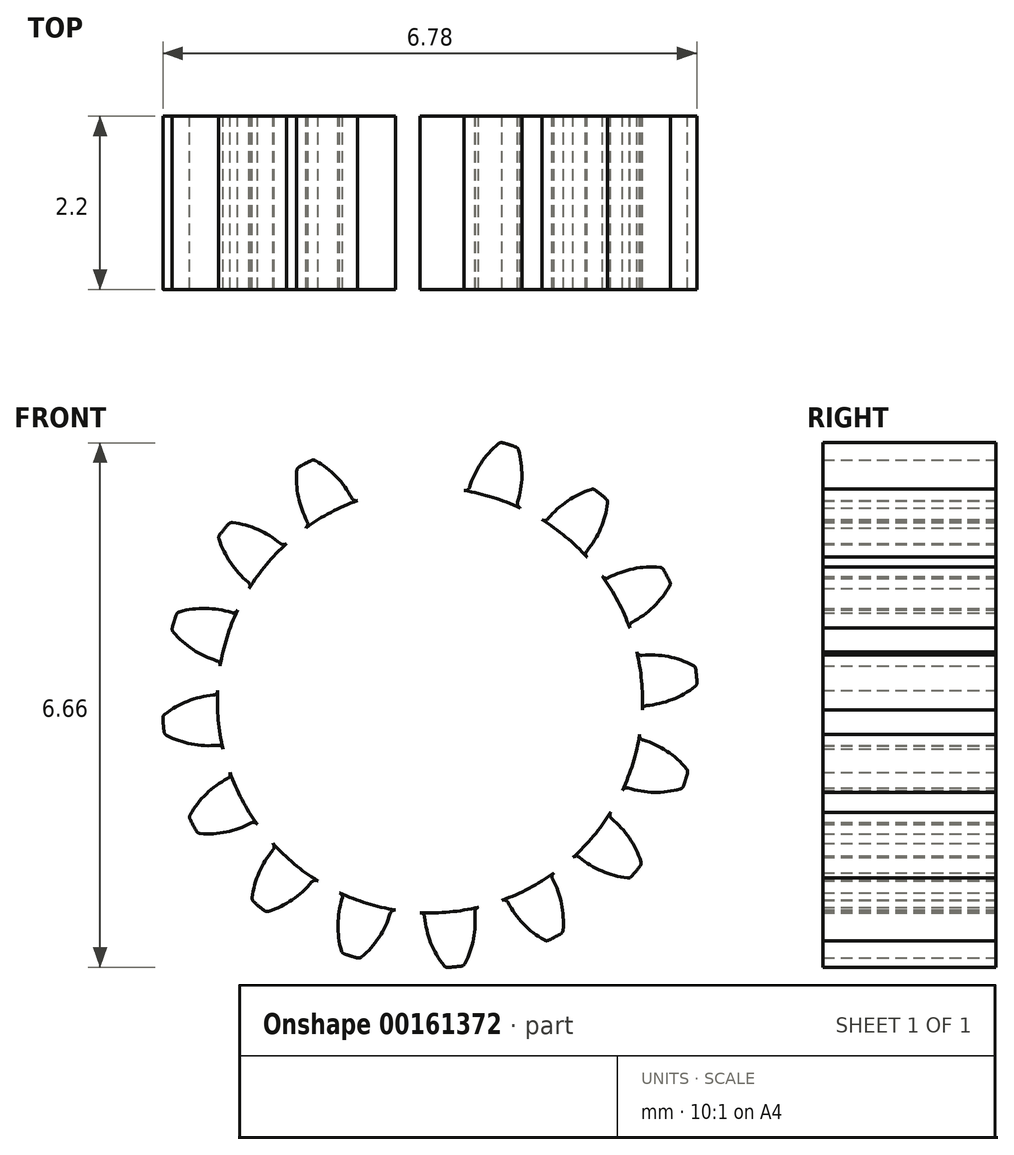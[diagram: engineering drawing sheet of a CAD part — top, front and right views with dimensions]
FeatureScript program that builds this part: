
annotation { "Feature Type Name" : "Feature", "Feature Type Description" : "" }
export const myFeature = defineFeature(function(context is Context, id is Id, definition is map)
    precondition{}
    {
        {
            var Q0;
            Q0=qCreatedBy(makeId("Front.planeOp"),FACE);
            var sketch = newSketch(context, id + "F0", { "sketchPlane" : qUnion([Q0])});
            skCircle(sketch, "E0", {"center": v(0, 0) * mm, "radius": 2.7 * mm, "construction": true});
            skCircle(sketch, "E1", {"center": v(0, 0) * mm, "radius": 3.05 * mm, "construction": true});
            skCircle(sketch, "E2", {"center": v(0, 0) * mm, "radius": 3.4 * mm, "construction": true});
            skLineSegment(sketch, "E3", {"start": v(0, 0) * mm, "end": v(0, 10.28) * mm, "construction": true});
            skLineSegment(sketch, "E4", {"start": v(0, 0) * mm, "end": v(-1.03, 11.12) * mm, "construction": true});
            skLineSegment(sketch, "E5", {"start": v(0, 3.05) * mm, "end": v(-15.76, 3.05) * mm, "construction": true});
            skLineSegment(sketch, "E6", {"start": v(0, 3.05) * mm, "end": v(-14.39, -2.19) * mm, "construction": true});
            skCircle(sketch, "E7", {"center": v(0, 3.05) * mm, "radius": 1.17 * mm, "construction": true});
            skCircle(sketch, "E8", {"center": v(-1.1, 2.65) * mm, "radius": 1.16 * mm, "construction": true});
            skArc(sketch, "E9", {"start": v(-0.18, 3.37) * mm, "mid": v(-0.01, 3.08) * mm, "end": v(0.07, 2.75) * mm});
            skArc(sketch, "E10.MirrorCS", {"start": v(-0.45, 3.34) * mm, "mid": v(-0.56, 3.03) * mm, "end": v(-0.57, 2.7) * mm});
            skArc(sketch, "E11", {"start": v(-0.4, 3.38) * mm, "mid": v(-0.31, 3.39) * mm, "end": v(-0.23, 3.4) * mm});
            skArc(sketch, "E12", {"start": v(-0.62, 2.63) * mm, "mid": v(0.25, -2.69) * mm, "end": v(0.12, 2.7) * mm});
            skPoint(sketch, "E13.visualSharp", {"position": v(-0.56, 2.64) * mm});
            skArc(sketch, "E13.filletArc", {"start": v(-0.62, 2.63) * mm, "mid": v(-0.58, 2.65) * mm, "end": v(-0.57, 2.7) * mm});
            skPoint(sketch, "E14.visualSharp", {"position": v(-0.43, 3.37) * mm});
            skArc(sketch, "E14.filletArc", {"start": v(-0.4, 3.38) * mm, "mid": v(-0.43, 3.37) * mm, "end": v(-0.45, 3.34) * mm});
            skPoint(sketch, "E15.visualSharp", {"position": v(-0.2, 3.4) * mm});
            skArc(sketch, "E15.filletArc", {"start": v(-0.18, 3.37) * mm, "mid": v(-0.2, 3.39) * mm, "end": v(-0.23, 3.4) * mm});
            skPoint(sketch, "E16.visualSharp", {"position": v(0.07, 2.7) * mm});
            skArc(sketch, "E16.filletArc", {"start": v(0.07, 2.75) * mm, "mid": v(0.08, 2.71) * mm, "end": v(0.12, 2.7) * mm});
            skArc(sketch, "E17.1.0", {"start": v(-1.58, 2.2) * mm, "mid": v(-1.55, 2.23) * mm, "end": v(-1.56, 2.27) * mm});
            skArc(sketch, "E17.1.1", {"start": v(-1.7, 2.92) * mm, "mid": v(-1.67, 2.59) * mm, "end": v(-1.56, 2.27) * mm});
            skArc(sketch, "E17.1.2", {"start": v(-1.66, 2.97) * mm, "mid": v(-1.68, 2.95) * mm, "end": v(-1.7, 2.92) * mm});
            skArc(sketch, "E17.1.3", {"start": v(-1.66, 2.97) * mm, "mid": v(-1.59, 3) * mm, "end": v(-1.5, 3.05) * mm});
            skArc(sketch, "E17.1.4", {"start": v(-1.45, 3.04) * mm, "mid": v(-1.48, 3.05) * mm, "end": v(-1.5, 3.05) * mm});
            skArc(sketch, "E17.1.5", {"start": v(-1.45, 3.04) * mm, "mid": v(-1.19, 2.84) * mm, "end": v(-1, 2.57) * mm});
            skArc(sketch, "E17.1.6", {"start": v(-1, 2.57) * mm, "mid": v(-0.96, 2.54) * mm, "end": v(-0.92, 2.54) * mm});
            skArc(sketch, "E17.2.0", {"start": v(-2.3, 1.42) * mm, "mid": v(-2.29, 1.46) * mm, "end": v(-2.3, 1.5) * mm});
            skArc(sketch, "E17.2.1", {"start": v(-2.68, 2.05) * mm, "mid": v(-2.53, 1.75) * mm, "end": v(-2.3, 1.5) * mm});
            skArc(sketch, "E17.2.2", {"start": v(-2.67, 2.1) * mm, "mid": v(-2.68, 2.08) * mm, "end": v(-2.68, 2.05) * mm});
            skArc(sketch, "E17.2.3", {"start": v(-2.67, 2.1) * mm, "mid": v(-2.62, 2.17) * mm, "end": v(-2.56, 2.24) * mm});
            skArc(sketch, "E17.2.4", {"start": v(-2.5, 2.26) * mm, "mid": v(-2.54, 2.25) * mm, "end": v(-2.56, 2.24) * mm});
            skArc(sketch, "E17.2.5", {"start": v(-2.5, 2.26) * mm, "mid": v(-2.18, 2.17) * mm, "end": v(-1.9, 2) * mm});
            skArc(sketch, "E17.2.6", {"start": v(-1.9, 2) * mm, "mid": v(-1.86, 1.98) * mm, "end": v(-1.82, 2) * mm});
            skArc(sketch, "E17.3.0", {"start": v(-2.66, 0.44) * mm, "mid": v(-2.67, 0.48) * mm, "end": v(-2.7, 0.5) * mm});
            skArc(sketch, "E17.3.1", {"start": v(-3.26, 0.87) * mm, "mid": v(-3, 0.65) * mm, "end": v(-2.7, 0.5) * mm});
            skArc(sketch, "E17.3.2", {"start": v(-3.27, 0.92) * mm, "mid": v(-3.27, 0.9) * mm, "end": v(-3.26, 0.87) * mm});
            skArc(sketch, "E17.3.3", {"start": v(-3.27, 0.92) * mm, "mid": v(-3.25, 1) * mm, "end": v(-3.22, 1.09) * mm});
            skArc(sketch, "E17.3.4", {"start": v(-3.18, 1.13) * mm, "mid": v(-3.2, 1.11) * mm, "end": v(-3.22, 1.09) * mm});
            skArc(sketch, "E17.3.5", {"start": v(-3.18, 1.13) * mm, "mid": v(-2.85, 1.17) * mm, "end": v(-2.52, 1.11) * mm});
            skArc(sketch, "E17.3.6", {"start": v(-2.52, 1.11) * mm, "mid": v(-2.48, 1.12) * mm, "end": v(-2.44, 1.15) * mm});
            skArc(sketch, "E17.4.0", {"start": v(-2.63, -0.62) * mm, "mid": v(-2.65, -0.58) * mm, "end": v(-2.7, -0.57) * mm});
            skArc(sketch, "E17.4.1", {"start": v(-3.34, -0.45) * mm, "mid": v(-3.03, -0.56) * mm, "end": v(-2.7, -0.57) * mm});
            skArc(sketch, "E17.4.2", {"start": v(-3.38, -0.4) * mm, "mid": v(-3.37, -0.43) * mm, "end": v(-3.34, -0.45) * mm});
            skArc(sketch, "E17.4.3", {"start": v(-3.38, -0.4) * mm, "mid": v(-3.39, -0.31) * mm, "end": v(-3.4, -0.23) * mm});
            skArc(sketch, "E17.4.4", {"start": v(-3.37, -0.18) * mm, "mid": v(-3.39, -0.2) * mm, "end": v(-3.4, -0.23) * mm});
            skArc(sketch, "E17.4.5", {"start": v(-3.37, -0.18) * mm, "mid": v(-3.08, -0.01) * mm, "end": v(-2.75, 0.07) * mm});
            skArc(sketch, "E17.4.6", {"start": v(-2.75, 0.07) * mm, "mid": v(-2.71, 0.08) * mm, "end": v(-2.7, 0.12) * mm});
            skArc(sketch, "E17.5.0", {"start": v(-2.2, -1.58) * mm, "mid": v(-2.23, -1.55) * mm, "end": v(-2.27, -1.56) * mm});
            skArc(sketch, "E17.5.1", {"start": v(-2.92, -1.7) * mm, "mid": v(-2.59, -1.67) * mm, "end": v(-2.27, -1.56) * mm});
            skArc(sketch, "E17.5.2", {"start": v(-2.97, -1.66) * mm, "mid": v(-2.95, -1.68) * mm, "end": v(-2.92, -1.7) * mm});
            skArc(sketch, "E17.5.3", {"start": v(-2.97, -1.66) * mm, "mid": v(-3, -1.59) * mm, "end": v(-3.05, -1.5) * mm});
            skArc(sketch, "E17.5.4", {"start": v(-3.04, -1.45) * mm, "mid": v(-3.05, -1.48) * mm, "end": v(-3.05, -1.5) * mm});
            skArc(sketch, "E17.5.5", {"start": v(-3.04, -1.45) * mm, "mid": v(-2.84, -1.19) * mm, "end": v(-2.57, -1) * mm});
            skArc(sketch, "E17.5.6", {"start": v(-2.57, -1) * mm, "mid": v(-2.54, -0.96) * mm, "end": v(-2.54, -0.92) * mm});
            skArc(sketch, "E17.6.0", {"start": v(-1.42, -2.3) * mm, "mid": v(-1.46, -2.29) * mm, "end": v(-1.5, -2.3) * mm});
            skArc(sketch, "E17.6.1", {"start": v(-2.05, -2.68) * mm, "mid": v(-1.75, -2.53) * mm, "end": v(-1.5, -2.3) * mm});
            skArc(sketch, "E17.6.2", {"start": v(-2.1, -2.67) * mm, "mid": v(-2.08, -2.68) * mm, "end": v(-2.05, -2.68) * mm});
            skArc(sketch, "E17.6.3", {"start": v(-2.1, -2.67) * mm, "mid": v(-2.17, -2.62) * mm, "end": v(-2.24, -2.56) * mm});
            skArc(sketch, "E17.6.4", {"start": v(-2.26, -2.5) * mm, "mid": v(-2.25, -2.54) * mm, "end": v(-2.24, -2.56) * mm});
            skArc(sketch, "E17.6.5", {"start": v(-2.26, -2.5) * mm, "mid": v(-2.17, -2.18) * mm, "end": v(-2, -1.9) * mm});
            skArc(sketch, "E17.6.6", {"start": v(-2, -1.9) * mm, "mid": v(-1.98, -1.86) * mm, "end": v(-2, -1.82) * mm});
            skArc(sketch, "E17.7.0", {"start": v(-0.44, -2.66) * mm, "mid": v(-0.48, -2.67) * mm, "end": v(-0.5, -2.7) * mm});
            skArc(sketch, "E17.7.1", {"start": v(-0.87, -3.26) * mm, "mid": v(-0.65, -3) * mm, "end": v(-0.5, -2.7) * mm});
            skArc(sketch, "E17.7.2", {"start": v(-0.92, -3.27) * mm, "mid": v(-0.9, -3.27) * mm, "end": v(-0.87, -3.26) * mm});
            skArc(sketch, "E17.7.3", {"start": v(-0.92, -3.27) * mm, "mid": v(-1, -3.25) * mm, "end": v(-1.09, -3.22) * mm});
            skArc(sketch, "E17.7.4", {"start": v(-1.13, -3.18) * mm, "mid": v(-1.11, -3.2) * mm, "end": v(-1.09, -3.22) * mm});
            skArc(sketch, "E17.7.5", {"start": v(-1.13, -3.18) * mm, "mid": v(-1.17, -2.85) * mm, "end": v(-1.11, -2.52) * mm});
            skArc(sketch, "E17.7.6", {"start": v(-1.11, -2.52) * mm, "mid": v(-1.12, -2.48) * mm, "end": v(-1.15, -2.44) * mm});
            skArc(sketch, "E17.8.0", {"start": v(0.62, -2.63) * mm, "mid": v(0.58, -2.65) * mm, "end": v(0.57, -2.7) * mm});
            skArc(sketch, "E17.8.1", {"start": v(0.45, -3.34) * mm, "mid": v(0.56, -3.03) * mm, "end": v(0.57, -2.7) * mm});
            skArc(sketch, "E17.8.2", {"start": v(0.4, -3.38) * mm, "mid": v(0.43, -3.37) * mm, "end": v(0.45, -3.34) * mm});
            skArc(sketch, "E17.8.3", {"start": v(0.4, -3.38) * mm, "mid": v(0.31, -3.39) * mm, "end": v(0.23, -3.4) * mm});
            skArc(sketch, "E17.8.4", {"start": v(0.18, -3.37) * mm, "mid": v(0.2, -3.39) * mm, "end": v(0.23, -3.4) * mm});
            skArc(sketch, "E17.8.5", {"start": v(0.18, -3.37) * mm, "mid": v(0.01, -3.08) * mm, "end": v(-0.07, -2.75) * mm});
            skArc(sketch, "E17.8.6", {"start": v(-0.07, -2.75) * mm, "mid": v(-0.08, -2.71) * mm, "end": v(-0.12, -2.7) * mm});
            skArc(sketch, "E17.9.0", {"start": v(1.58, -2.2) * mm, "mid": v(1.55, -2.23) * mm, "end": v(1.56, -2.27) * mm});
            skArc(sketch, "E17.9.1", {"start": v(1.7, -2.92) * mm, "mid": v(1.67, -2.59) * mm, "end": v(1.56, -2.27) * mm});
            skArc(sketch, "E17.9.2", {"start": v(1.66, -2.97) * mm, "mid": v(1.68, -2.95) * mm, "end": v(1.7, -2.92) * mm});
            skArc(sketch, "E17.9.3", {"start": v(1.66, -2.97) * mm, "mid": v(1.59, -3) * mm, "end": v(1.5, -3.05) * mm});
            skArc(sketch, "E17.9.4", {"start": v(1.45, -3.04) * mm, "mid": v(1.48, -3.05) * mm, "end": v(1.5, -3.05) * mm});
            skArc(sketch, "E17.9.5", {"start": v(1.45, -3.04) * mm, "mid": v(1.19, -2.84) * mm, "end": v(1, -2.57) * mm});
            skArc(sketch, "E17.9.6", {"start": v(1, -2.57) * mm, "mid": v(0.96, -2.54) * mm, "end": v(0.92, -2.54) * mm});
            skArc(sketch, "E17.10.0", {"start": v(2.3, -1.42) * mm, "mid": v(2.29, -1.46) * mm, "end": v(2.3, -1.5) * mm});
            skArc(sketch, "E17.10.1", {"start": v(2.68, -2.05) * mm, "mid": v(2.53, -1.75) * mm, "end": v(2.3, -1.5) * mm});
            skArc(sketch, "E17.10.2", {"start": v(2.67, -2.1) * mm, "mid": v(2.68, -2.08) * mm, "end": v(2.68, -2.05) * mm});
            skArc(sketch, "E17.10.3", {"start": v(2.67, -2.1) * mm, "mid": v(2.62, -2.17) * mm, "end": v(2.56, -2.24) * mm});
            skArc(sketch, "E17.10.4", {"start": v(2.5, -2.26) * mm, "mid": v(2.54, -2.25) * mm, "end": v(2.56, -2.24) * mm});
            skArc(sketch, "E17.10.5", {"start": v(2.5, -2.26) * mm, "mid": v(2.18, -2.17) * mm, "end": v(1.9, -2) * mm});
            skArc(sketch, "E17.10.6", {"start": v(1.9, -2) * mm, "mid": v(1.86, -1.98) * mm, "end": v(1.82, -2) * mm});
            skArc(sketch, "E17.11.0", {"start": v(2.66, -0.44) * mm, "mid": v(2.67, -0.48) * mm, "end": v(2.7, -0.5) * mm});
            skArc(sketch, "E17.11.1", {"start": v(3.26, -0.87) * mm, "mid": v(3, -0.65) * mm, "end": v(2.7, -0.5) * mm});
            skArc(sketch, "E17.11.2", {"start": v(3.27, -0.92) * mm, "mid": v(3.27, -0.9) * mm, "end": v(3.26, -0.87) * mm});
            skArc(sketch, "E17.11.3", {"start": v(3.27, -0.92) * mm, "mid": v(3.25, -1) * mm, "end": v(3.22, -1.09) * mm});
            skArc(sketch, "E17.11.4", {"start": v(3.18, -1.13) * mm, "mid": v(3.2, -1.11) * mm, "end": v(3.22, -1.09) * mm});
            skArc(sketch, "E17.11.5", {"start": v(3.18, -1.13) * mm, "mid": v(2.85, -1.17) * mm, "end": v(2.52, -1.11) * mm});
            skArc(sketch, "E17.11.6", {"start": v(2.52, -1.11) * mm, "mid": v(2.48, -1.12) * mm, "end": v(2.44, -1.15) * mm});
            skArc(sketch, "E17.12.0", {"start": v(2.63, 0.62) * mm, "mid": v(2.65, 0.58) * mm, "end": v(2.7, 0.57) * mm});
            skArc(sketch, "E17.12.1", {"start": v(3.34, 0.45) * mm, "mid": v(3.03, 0.56) * mm, "end": v(2.7, 0.57) * mm});
            skArc(sketch, "E17.12.2", {"start": v(3.38, 0.4) * mm, "mid": v(3.37, 0.43) * mm, "end": v(3.34, 0.45) * mm});
            skArc(sketch, "E17.12.3", {"start": v(3.38, 0.4) * mm, "mid": v(3.39, 0.31) * mm, "end": v(3.4, 0.23) * mm});
            skArc(sketch, "E17.12.4", {"start": v(3.37, 0.18) * mm, "mid": v(3.39, 0.2) * mm, "end": v(3.4, 0.23) * mm});
            skArc(sketch, "E17.12.5", {"start": v(3.37, 0.18) * mm, "mid": v(3.08, 0.01) * mm, "end": v(2.75, -0.07) * mm});
            skArc(sketch, "E17.12.6", {"start": v(2.75, -0.07) * mm, "mid": v(2.71, -0.08) * mm, "end": v(2.7, -0.12) * mm});
            skArc(sketch, "E17.13.0", {"start": v(2.2, 1.58) * mm, "mid": v(2.23, 1.55) * mm, "end": v(2.27, 1.56) * mm});
            skArc(sketch, "E17.13.1", {"start": v(2.92, 1.7) * mm, "mid": v(2.59, 1.67) * mm, "end": v(2.27, 1.56) * mm});
            skArc(sketch, "E17.13.2", {"start": v(2.97, 1.66) * mm, "mid": v(2.95, 1.68) * mm, "end": v(2.92, 1.7) * mm});
            skArc(sketch, "E17.13.3", {"start": v(2.97, 1.66) * mm, "mid": v(3, 1.59) * mm, "end": v(3.05, 1.5) * mm});
            skArc(sketch, "E17.13.4", {"start": v(3.04, 1.45) * mm, "mid": v(3.05, 1.48) * mm, "end": v(3.05, 1.5) * mm});
            skArc(sketch, "E17.13.5", {"start": v(3.04, 1.45) * mm, "mid": v(2.84, 1.19) * mm, "end": v(2.57, 1) * mm});
            skArc(sketch, "E17.13.6", {"start": v(2.57, 1) * mm, "mid": v(2.54, 0.96) * mm, "end": v(2.54, 0.92) * mm});
            skArc(sketch, "E17.14.0", {"start": v(1.42, 2.3) * mm, "mid": v(1.46, 2.29) * mm, "end": v(1.5, 2.3) * mm});
            skArc(sketch, "E17.14.1", {"start": v(2.05, 2.68) * mm, "mid": v(1.75, 2.53) * mm, "end": v(1.5, 2.3) * mm});
            skArc(sketch, "E17.14.2", {"start": v(2.1, 2.67) * mm, "mid": v(2.08, 2.68) * mm, "end": v(2.05, 2.68) * mm});
            skArc(sketch, "E17.14.3", {"start": v(2.1, 2.67) * mm, "mid": v(2.17, 2.62) * mm, "end": v(2.24, 2.56) * mm});
            skArc(sketch, "E17.14.4", {"start": v(2.26, 2.5) * mm, "mid": v(2.25, 2.54) * mm, "end": v(2.24, 2.56) * mm});
            skArc(sketch, "E17.14.5", {"start": v(2.26, 2.5) * mm, "mid": v(2.17, 2.18) * mm, "end": v(2, 1.9) * mm});
            skArc(sketch, "E17.14.6", {"start": v(2, 1.9) * mm, "mid": v(1.98, 1.86) * mm, "end": v(2, 1.82) * mm});
            skArc(sketch, "E17.15.0", {"start": v(0.44, 2.66) * mm, "mid": v(0.48, 2.67) * mm, "end": v(0.5, 2.7) * mm});
            skArc(sketch, "E17.15.1", {"start": v(0.87, 3.26) * mm, "mid": v(0.65, 3) * mm, "end": v(0.5, 2.7) * mm});
            skArc(sketch, "E17.15.2", {"start": v(0.92, 3.27) * mm, "mid": v(0.9, 3.27) * mm, "end": v(0.87, 3.26) * mm});
            skArc(sketch, "E17.15.3", {"start": v(0.92, 3.27) * mm, "mid": v(1, 3.25) * mm, "end": v(1.09, 3.22) * mm});
            skArc(sketch, "E17.15.4", {"start": v(1.13, 3.18) * mm, "mid": v(1.11, 3.2) * mm, "end": v(1.09, 3.22) * mm});
            skArc(sketch, "E17.15.5", {"start": v(1.13, 3.18) * mm, "mid": v(1.17, 2.85) * mm, "end": v(1.11, 2.52) * mm});
            skArc(sketch, "E17.15.6", {"start": v(1.11, 2.52) * mm, "mid": v(1.12, 2.48) * mm, "end": v(1.15, 2.44) * mm});
            skSolve(sketch);
        }
        {
            var Q0;
            Q0=makeQuery(id+"F0.imprint","IMPRINT",FACE,{"disambiguationData":[TD([[makeQuery(id+"F0.imprint","IMPRINT",EDGE,{"derivedFrom":sQuery(id+"F0.wireOp",EDGE,"E9")}),-1.0]])]});
            var Q1;
            {var subQ0=sQuery(id+"F0.wireOp",EDGE,"E17.1.0");Q1=makeQuery(id+"F0.imprint","IMPRINT",FACE,{"disambiguationData":[TD([[makeQuery(id+"F0.imprint","IMPRINT",EDGE,{"derivedFrom":subQ0}),-1.0]])]});}
            var Q2;
            {var subQ0=sQuery(id+"F0.wireOp",EDGE,"E17.2.0");Q2=makeQuery(id+"F0.imprint","IMPRINT",FACE,{"disambiguationData":[TD([[makeQuery(id+"F0.imprint","IMPRINT",EDGE,{"derivedFrom":subQ0}),-1.0]])]});}
            var Q3;
            {var subQ0=sQuery(id+"F0.wireOp",EDGE,"E17.3.0");Q3=makeQuery(id+"F0.imprint","IMPRINT",FACE,{"disambiguationData":[TD([[makeQuery(id+"F0.imprint","IMPRINT",EDGE,{"derivedFrom":subQ0}),-1.0]])]});}
            var Q4;
            {var subQ0=sQuery(id+"F0.wireOp",EDGE,"E17.4.0");Q4=makeQuery(id+"F0.imprint","IMPRINT",FACE,{"disambiguationData":[TD([[makeQuery(id+"F0.imprint","IMPRINT",EDGE,{"derivedFrom":subQ0}),-1.0]])]});}
            var Q5;
            {var subQ0=sQuery(id+"F0.wireOp",EDGE,"E17.16.0");Q5=makeQuery(id+"F0.imprint","IMPRINT",FACE,{"disambiguationData":[TD([[makeQuery(id+"F0.imprint","IMPRINT",EDGE,{"derivedFrom":subQ0}),-1.0]])]});}
            var Q6;
            {var subQ0=sQuery(id+"F0.wireOp",EDGE,"E17.15.0");Q6=makeQuery(id+"F0.imprint","IMPRINT",FACE,{"disambiguationData":[TD([[makeQuery(id+"F0.imprint","IMPRINT",EDGE,{"derivedFrom":subQ0}),-1.0]])]});}
            var Q7;
            {var subQ1=sQuery(id+"F0.wireOp",EDGE,"E17.14.0");Q7=makeQuery(id+"F0.imprint","IMPRINT",FACE,{"disambiguationData":[TD([[makeQuery(id+"F0.imprint","IMPRINT",EDGE,{"derivedFrom":subQ1}),-1.0]])]});}
            var Q8;
            {var subQ0=sQuery(id+"F0.wireOp",EDGE,"E17.13.0");Q8=makeQuery(id+"F0.imprint","IMPRINT",FACE,{"disambiguationData":[TD([[makeQuery(id+"F0.imprint","IMPRINT",EDGE,{"derivedFrom":subQ0}),-1.0]])]});}
            var Q9;
            {var subQ1=sQuery(id+"F0.wireOp",EDGE,"E17.12.0");Q9=makeQuery(id+"F0.imprint","IMPRINT",FACE,{"disambiguationData":[TD([[makeQuery(id+"F0.imprint","IMPRINT",EDGE,{"derivedFrom":subQ1}),-1.0]])]});}
            var Q10;
            {var subQ0=sQuery(id+"F0.wireOp",EDGE,"E17.11.0");Q10=makeQuery(id+"F0.imprint","IMPRINT",FACE,{"disambiguationData":[TD([[makeQuery(id+"F0.imprint","IMPRINT",EDGE,{"derivedFrom":subQ0}),-1.0]])]});}
            var Q11;
            {var subQ0=sQuery(id+"F0.wireOp",EDGE,"E17.10.0");Q11=makeQuery(id+"F0.imprint","IMPRINT",FACE,{"disambiguationData":[TD([[makeQuery(id+"F0.imprint","IMPRINT",EDGE,{"derivedFrom":subQ0}),-1.0]])]});}
            var Q12;
            {var subQ0=sQuery(id+"F0.wireOp",EDGE,"E17.9.0");Q12=makeQuery(id+"F0.imprint","IMPRINT",FACE,{"disambiguationData":[TD([[makeQuery(id+"F0.imprint","IMPRINT",EDGE,{"derivedFrom":subQ0}),-1.0]])]});}
            var Q13;
            {var subQ0=sQuery(id+"F0.wireOp",EDGE,"E17.8.0");Q13=makeQuery(id+"F0.imprint","IMPRINT",FACE,{"disambiguationData":[TD([[makeQuery(id+"F0.imprint","IMPRINT",EDGE,{"derivedFrom":subQ0}),-1.0]])]});}
            var Q14;
            {var subQ0=sQuery(id+"F0.wireOp",EDGE,"E17.7.0");Q14=makeQuery(id+"F0.imprint","IMPRINT",FACE,{"disambiguationData":[TD([[makeQuery(id+"F0.imprint","IMPRINT",EDGE,{"derivedFrom":subQ0}),-1.0]])]});}
            var Q15;
            {var subQ0=sQuery(id+"F0.wireOp",EDGE,"E17.6.0");Q15=makeQuery(id+"F0.imprint","IMPRINT",FACE,{"disambiguationData":[TD([[makeQuery(id+"F0.imprint","IMPRINT",EDGE,{"derivedFrom":subQ0}),-1.0]])]});}
            var Q16;
            {var subQ0=sQuery(id+"F0.wireOp",EDGE,"E17.5.0");Q16=makeQuery(id+"F0.imprint","IMPRINT",FACE,{"disambiguationData":[TD([[makeQuery(id+"F0.imprint","IMPRINT",EDGE,{"derivedFrom":subQ0}),-1.0]])]});}
            extrude(context, id + "F1", {"entities" : qUnion([Q0, Q1, Q2, Q3, Q4, Q5, Q6, Q7, Q8, Q9, Q10, Q11, Q12, Q13, Q14, Q15, Q16]), "depth" : 2.2 * mm});
        }
        {
            var Q0;
            Q0=makeQuery(id+"F1.opExtrude","CAP_FACE",FACE,{"disambiguationData":[OSD([sQuery(id+"F0.wireOp",EDGE,"E9"),sQuery(id+"F0.wireOp",EDGE,"E10.MirrorCS"),sQuery(id+"F0.wireOp",EDGE,"E11"),sQuery(id+"F0.wireOp",EDGE,"E12"),sQuery(id+"F0.wireOp",EDGE,"E13.filletArc"),sQuery(id+"F0.wireOp",EDGE,"E14.filletArc"),sQuery(id+"F0.wireOp",EDGE,"E15.filletArc"),sQuery(id+"F0.wireOp",EDGE,"E16.filletArc"),sQuery(id+"F0.wireOp",EDGE,"E17.1.0"),sQuery(id+"F0.wireOp",EDGE,"E17.1.1"),sQuery(id+"F0.wireOp",EDGE,"E17.1.2"),sQuery(id+"F0.wireOp",EDGE,"E17.1.3"),sQuery(id+"F0.wireOp",EDGE,"E17.1.4"),sQuery(id+"F0.wireOp",EDGE,"E17.1.5"),sQuery(id+"F0.wireOp",EDGE,"E17.1.6"),sQuery(id+"F0.wireOp",EDGE,"E17.2.0"),sQuery(id+"F0.wireOp",EDGE,"E17.2.1"),sQuery(id+"F0.wireOp",EDGE,"E17.2.2"),sQuery(id+"F0.wireOp",EDGE,"E17.2.3"),sQuery(id+"F0.wireOp",EDGE,"E17.2.4"),sQuery(id+"F0.wireOp",EDGE,"E17.2.5"),sQuery(id+"F0.wireOp",EDGE,"E17.2.6"),sQuery(id+"F0.wireOp",EDGE,"E17.3.0"),sQuery(id+"F0.wireOp",EDGE,"E17.3.1"),sQuery(id+"F0.wireOp",EDGE,"E17.3.2"),sQuery(id+"F0.wireOp",EDGE,"E17.3.3"),sQuery(id+"F0.wireOp",EDGE,"E17.3.4"),sQuery(id+"F0.wireOp",EDGE,"E17.3.5"),sQuery(id+"F0.wireOp",EDGE,"E17.3.6"),sQuery(id+"F0.wireOp",EDGE,"E17.4.0"),sQuery(id+"F0.wireOp",EDGE,"E17.4.1"),sQuery(id+"F0.wireOp",EDGE,"E17.4.2"),sQuery(id+"F0.wireOp",EDGE,"E17.4.3"),sQuery(id+"F0.wireOp",EDGE,"E17.4.4"),sQuery(id+"F0.wireOp",EDGE,"E17.4.5"),sQuery(id+"F0.wireOp",EDGE,"E17.4.6"),sQuery(id+"F0.wireOp",EDGE,"E17.5.0"),sQuery(id+"F0.wireOp",EDGE,"E17.5.1"),sQuery(id+"F0.wireOp",EDGE,"E17.5.2"),sQuery(id+"F0.wireOp",EDGE,"E17.5.3"),sQuery(id+"F0.wireOp",EDGE,"E17.5.4"),sQuery(id+"F0.wireOp",EDGE,"E17.5.5"),sQuery(id+"F0.wireOp",EDGE,"E17.5.6"),sQuery(id+"F0.wireOp",EDGE,"E17.6.0"),sQuery(id+"F0.wireOp",EDGE,"E17.6.1"),sQuery(id+"F0.wireOp",EDGE,"E17.6.2"),sQuery(id+"F0.wireOp",EDGE,"E17.6.3"),sQuery(id+"F0.wireOp",EDGE,"E17.6.4"),sQuery(id+"F0.wireOp",EDGE,"E17.6.5"),sQuery(id+"F0.wireOp",EDGE,"E17.6.6"),sQuery(id+"F0.wireOp",EDGE,"E17.7.0"),sQuery(id+"F0.wireOp",EDGE,"E17.7.1"),sQuery(id+"F0.wireOp",EDGE,"E17.7.2"),sQuery(id+"F0.wireOp",EDGE,"E17.7.3"),sQuery(id+"F0.wireOp",EDGE,"E17.7.4"),sQuery(id+"F0.wireOp",EDGE,"E17.7.5"),sQuery(id+"F0.wireOp",EDGE,"E17.7.6"),sQuery(id+"F0.wireOp",EDGE,"E17.8.0"),sQuery(id+"F0.wireOp",EDGE,"E17.8.1"),sQuery(id+"F0.wireOp",EDGE,"E17.8.2"),sQuery(id+"F0.wireOp",EDGE,"E17.8.3"),sQuery(id+"F0.wireOp",EDGE,"E17.8.4"),sQuery(id+"F0.wireOp",EDGE,"E17.8.5"),sQuery(id+"F0.wireOp",EDGE,"E17.8.6"),sQuery(id+"F0.wireOp",EDGE,"E17.9.0"),sQuery(id+"F0.wireOp",EDGE,"E17.9.1"),sQuery(id+"F0.wireOp",EDGE,"E17.9.2"),sQuery(id+"F0.wireOp",EDGE,"E17.9.3"),sQuery(id+"F0.wireOp",EDGE,"E17.9.4"),sQuery(id+"F0.wireOp",EDGE,"E17.9.5"),sQuery(id+"F0.wireOp",EDGE,"E17.9.6"),sQuery(id+"F0.wireOp",EDGE,"E17.10.0"),sQuery(id+"F0.wireOp",EDGE,"E17.10.1"),sQuery(id+"F0.wireOp",EDGE,"E17.10.2"),sQuery(id+"F0.wireOp",EDGE,"E17.10.3"),sQuery(id+"F0.wireOp",EDGE,"E17.10.4"),sQuery(id+"F0.wireOp",EDGE,"E17.10.5"),sQuery(id+"F0.wireOp",EDGE,"E17.10.6"),sQuery(id+"F0.wireOp",EDGE,"E17.11.0"),sQuery(id+"F0.wireOp",EDGE,"E17.11.1"),sQuery(id+"F0.wireOp",EDGE,"E17.11.2"),sQuery(id+"F0.wireOp",EDGE,"E17.11.3"),sQuery(id+"F0.wireOp",EDGE,"E17.11.4"),sQuery(id+"F0.wireOp",EDGE,"E17.11.5"),sQuery(id+"F0.wireOp",EDGE,"E17.11.6"),sQuery(id+"F0.wireOp",EDGE,"E17.12.0"),sQuery(id+"F0.wireOp",EDGE,"E17.12.1"),sQuery(id+"F0.wireOp",EDGE,"E17.12.2"),sQuery(id+"F0.wireOp",EDGE,"E17.12.3"),sQuery(id+"F0.wireOp",EDGE,"E17.12.4"),sQuery(id+"F0.wireOp",EDGE,"E17.12.5"),sQuery(id+"F0.wireOp",EDGE,"E17.12.6"),sQuery(id+"F0.wireOp",EDGE,"E17.13.0"),sQuery(id+"F0.wireOp",EDGE,"E17.13.1"),sQuery(id+"F0.wireOp",EDGE,"E17.13.2"),sQuery(id+"F0.wireOp",EDGE,"E17.13.3"),sQuery(id+"F0.wireOp",EDGE,"E17.13.4"),sQuery(id+"F0.wireOp",EDGE,"E17.13.5"),sQuery(id+"F0.wireOp",EDGE,"E17.13.6"),sQuery(id+"F0.wireOp",EDGE,"E17.14.0"),sQuery(id+"F0.wireOp",EDGE,"E17.14.1"),sQuery(id+"F0.wireOp",EDGE,"E17.14.2"),sQuery(id+"F0.wireOp",EDGE,"E17.14.3"),sQuery(id+"F0.wireOp",EDGE,"E17.14.4"),sQuery(id+"F0.wireOp",EDGE,"E17.14.5"),sQuery(id+"F0.wireOp",EDGE,"E17.14.6"),sQuery(id+"F0.wireOp",EDGE,"E17.15.0"),sQuery(id+"F0.wireOp",EDGE,"E17.15.1"),sQuery(id+"F0.wireOp",EDGE,"E17.15.2"),sQuery(id+"F0.wireOp",EDGE,"E17.15.3"),sQuery(id+"F0.wireOp",EDGE,"E17.15.4"),sQuery(id+"F0.wireOp",EDGE,"E17.15.5"),sQuery(id+"F0.wireOp",EDGE,"E17.15.6"),sQuery(id+"F0.wireOp",EDGE,"E17.16.0"),sQuery(id+"F0.wireOp",EDGE,"E17.16.1"),sQuery(id+"F0.wireOp",EDGE,"E17.16.2"),sQuery(id+"F0.wireOp",EDGE,"E17.16.3"),sQuery(id+"F0.wireOp",EDGE,"E17.16.4"),sQuery(id+"F0.wireOp",EDGE,"E17.16.5"),sQuery(id+"F0.wireOp",EDGE,"E17.16.6")])],"isStart":false});
            var sketch = newSketch(context, id + "F2", { "sketchPlane" : qUnion([Q0])});
            skCircle(sketch, "E18", {"center": v(0, 0) * mm, "radius": 1 * mm});
            skSolve(sketch);
        }
        {
            var Q0;
            Q0=qSketchRegion(id+"F2",true);
            extrude(context, id + "F3", {"entities" : qUnion([Q0]), "operationType" : NewBodyOperationType.REMOVE, "endBound" : BoundingType.THROUGH_ALL, "oppositeDirection" : true, "depth" : 25 * mm});
        }
    });
